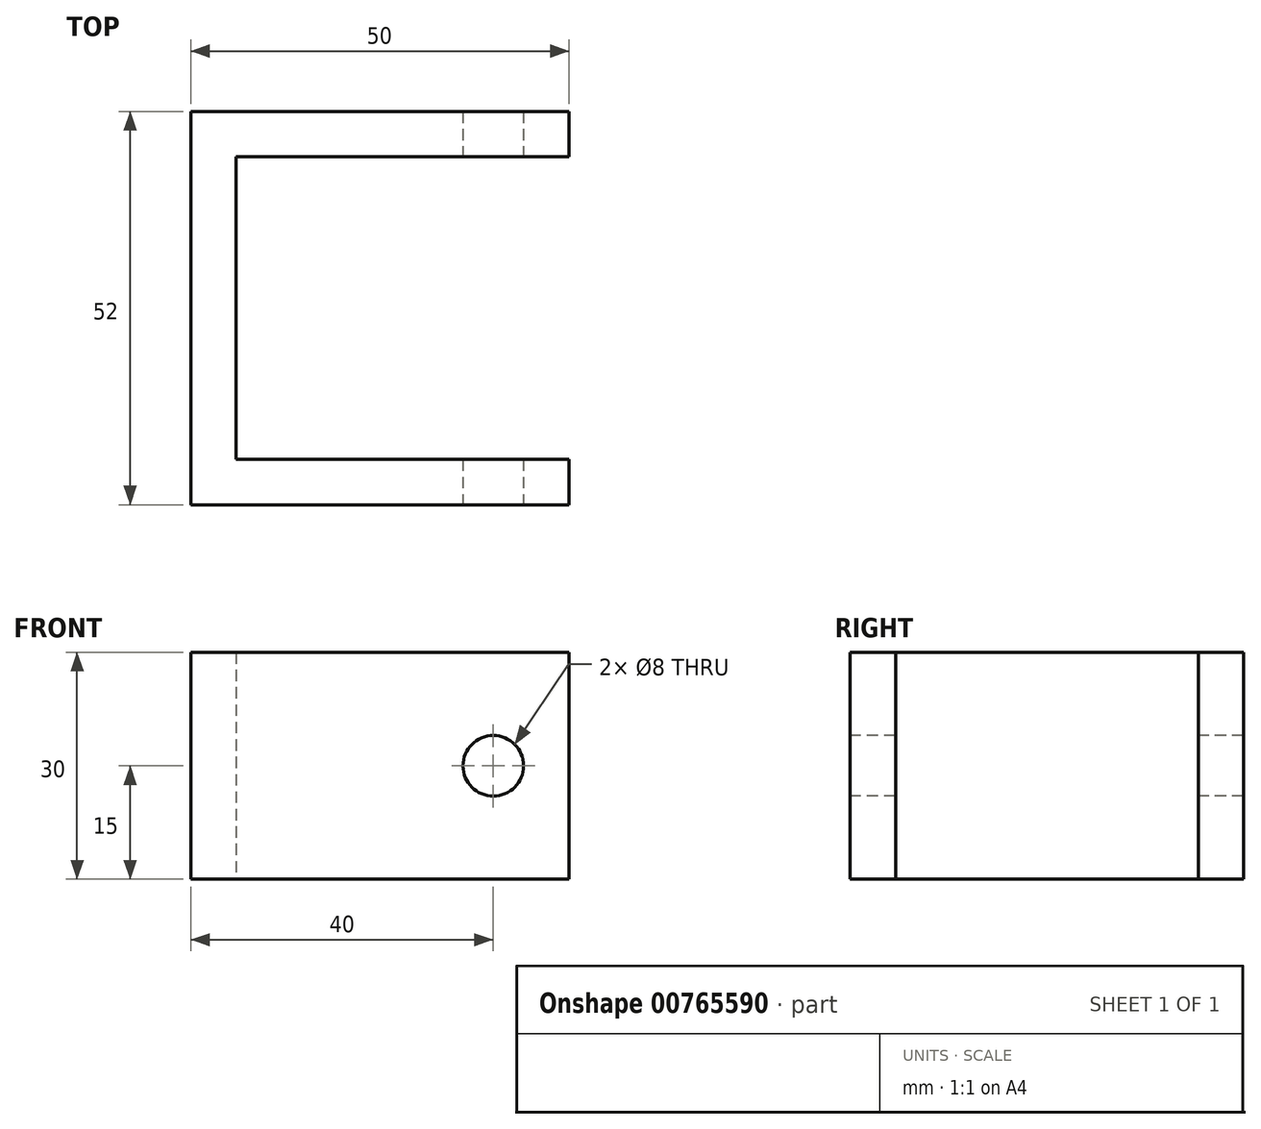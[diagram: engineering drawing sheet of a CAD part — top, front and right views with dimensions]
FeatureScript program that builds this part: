
annotation { "Feature Type Name" : "Feature", "Feature Type Description" : "" }
export const myFeature = defineFeature(function(context is Context, id is Id, definition is map)
    precondition{}
    {
        {
            var Q0;
            Q0=qCreatedBy(makeId("Top.planeOp"),FACE);
            var sketch = newSketch(context, id + "F0", { "sketchPlane" : qUnion([Q0])});
            skLineSegment(sketch, "E0.bottom", {"start": v(0, 0) * mm, "end": v(6, 0) * mm});
            skLineSegment(sketch, "E0.top", {"start": v(0, 40) * mm, "end": v(6, 40) * mm});
            skLineSegment(sketch, "E0.left", {"start": v(0, 0) * mm, "end": v(0, 40) * mm});
            skLineSegment(sketch, "E0.right", {"start": v(6, 0) * mm, "end": v(6, 40) * mm});
            skLineSegment(sketch, "E1.bottom", {"start": v(0, 40) * mm, "end": v(50, 40) * mm});
            skLineSegment(sketch, "E1.top", {"start": v(0, 46) * mm, "end": v(50, 46) * mm});
            skLineSegment(sketch, "E1.left", {"start": v(0, 40) * mm, "end": v(0, 46) * mm});
            skLineSegment(sketch, "E1.right", {"start": v(50, 40) * mm, "end": v(50, 46) * mm});
            skLineSegment(sketch, "E2.bottom", {"start": v(0, 0) * mm, "end": v(50, 0) * mm});
            skLineSegment(sketch, "E2.top", {"start": v(0, -6) * mm, "end": v(50, -6) * mm});
            skLineSegment(sketch, "E2.left", {"start": v(0, 0) * mm, "end": v(0, -6) * mm});
            skLineSegment(sketch, "E2.right", {"start": v(50, 0) * mm, "end": v(50, -6) * mm});
            skSolve(sketch);
        }
        {
            var Q0;
            Q0 = qSketchRegion(id + "F0", true);
            extrude(context, id + "F1", {"entities" : qUnion([Q0]), "depth" : 30 * mm, "offsetDistance" : 25 * mm});
        }
        {
            var Q0;
            Q0=makeQuery(id+"F1.opExtrude","SWEPT_FACE",FACE,{"disambiguationData":[OSD([sQuery(id+"F0.wireOp",EDGE,"E2.top")])]});
            var sketch = newSketch(context, id + "F2", { "sketchPlane" : qUnion([Q0])});
            skLineSegment(sketch, "E3", {"start": v(50, 15) * mm, "end": v(40, 15) * mm});
            skCircle(sketch, "E4", {"center": v(40, 15) * mm, "radius": 4 * mm});
            skSolve(sketch);
        }
        {
            var Q0;
            Q0 = qSketchRegion(id + "F2", true);
            extrude(context, id + "F3", {"entities" : qUnion([Q0]), "operationType" : NewBodyOperationType.REMOVE, "endBound" : BoundingType.THROUGH_ALL, "oppositeDirection" : true, "depth" : 25 * mm, "offsetDistance" : 25 * mm});
        }
    });
